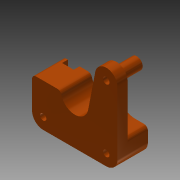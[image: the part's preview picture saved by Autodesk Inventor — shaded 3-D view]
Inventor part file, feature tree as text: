
AUTODESK INVENTOR PART (.ipt)
format: ipt  version: 2013 (Build 170138000, 138)  size: 176,640 bytes
history: native  units: in
note: dims shown in document units (in); Inventor stores cm internally (conversion verified against a paired STEP export)
features: sketch x11, other x2, extrude x1
ambient origin geometry x8: Origin, YZ Plane, XZ Plane, XY Plane, X Axis, Y Axis, Z Axis, Center Point
bodies: Solid1 (feature_tree)
feature tree (14):
  extrude  "EXTRUDER BODY.ipt"  [1 undecoded]
  other  "Solid1::EXTRUDER BODY.ipt"
  other  "TaggingFeature1"
  sketch  "Sketch1"  dims[d0=0.3937in]
  sketch  "Sketch2"  dims[d2=1.2205in d3=1.6535in d4=0.122in d5=0.5906in d6=0.0in d7=0.425in d9=0.3346in d11=0.0689in d12=0.0787in d13=0.3937in d14=0.0in d15=0.2469in d16=0.4803in d17=0.2913in d18=0.0in d19=0.6378in d21=0.1575in d22=0.0in d24=0.6378in d27=0.0591in d28=0.0in d29=0.1614in d32=0.0in d33=1.2205in d34=0.2362in d36=0.0in d37=0.2244in d38=0.6102in d39=0.3937in d40=0.0in d41=0.126in d43=0.1181in d44=0.0in d45=0.2165in d46=0.0787in d47=0.2283in d50=0.3937in d51=0.0in d52=0.126in d55=0.0in]
  sketch  "Sketch3"
  sketch  "Sketch4"
  sketch  "Sketch5"
  sketch  "Sketch6"
  sketch  "Sketch7"
  sketch  "Sketch8"
  sketch  "Sketch9"
  sketch  "Sketch10"
  sketch  "Sketch11"
note: 1 required parameter value undecoded (feature->parameter linkage not recoverable at this tier; creation-order binding heuristic only, values carry confidence <= 0.55)
